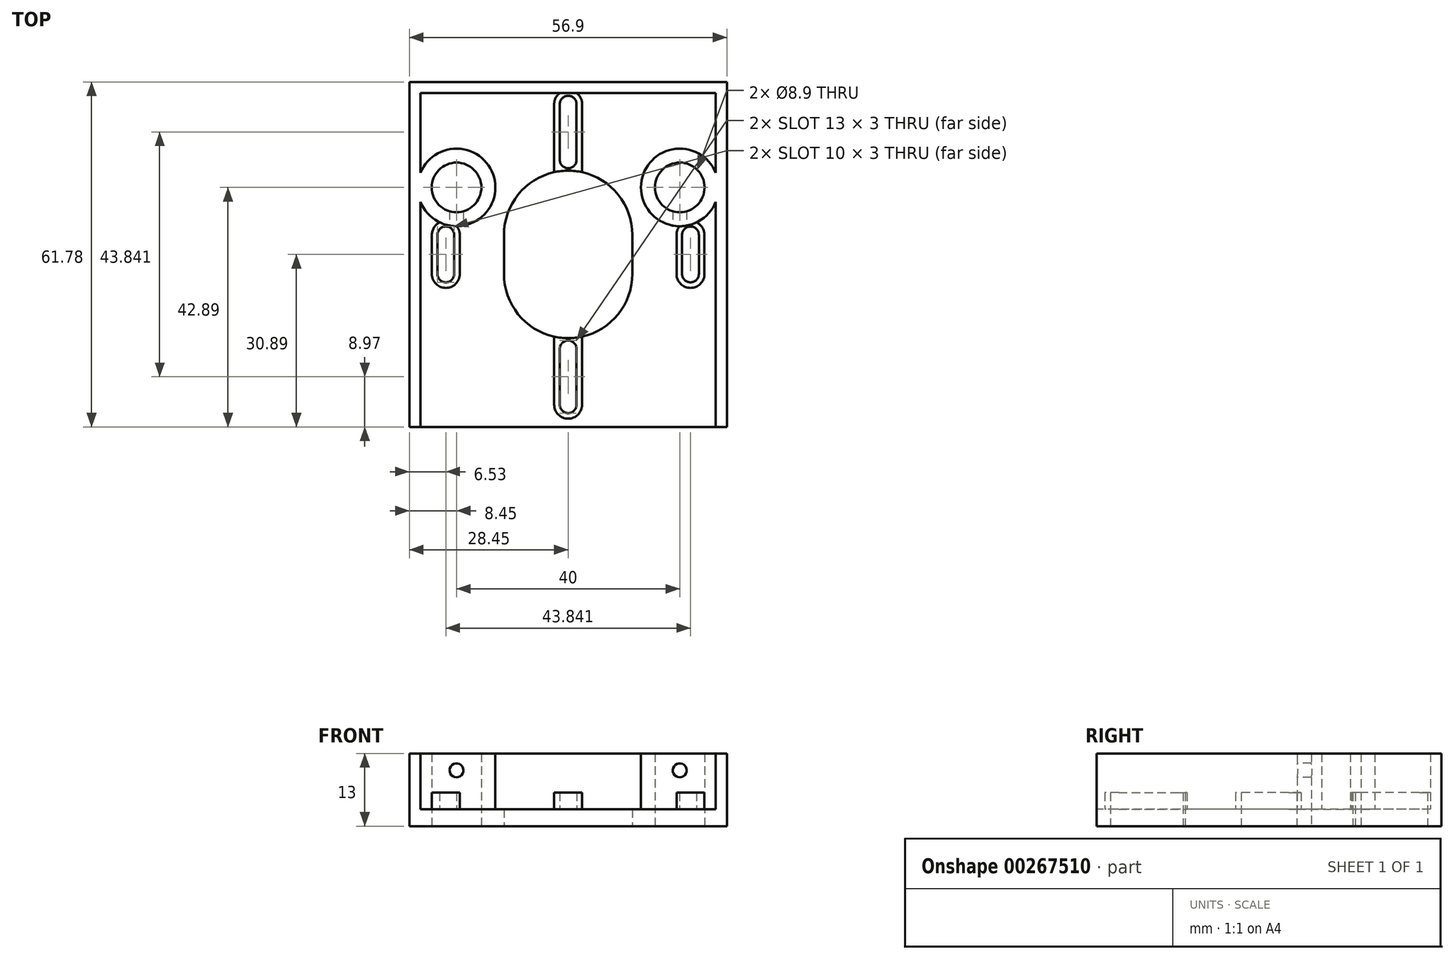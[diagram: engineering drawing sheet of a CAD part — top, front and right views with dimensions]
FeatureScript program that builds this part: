
annotation { "Feature Type Name" : "Feature", "Feature Type Description" : "" }
export const myFeature = defineFeature(function(context is Context, id is Id, definition is map)
    precondition{}
    {
        {
            var Q0;
            Q0=qCreatedBy(makeId("Top.planeOp"),FACE);
            var sketch = newSketch(context, id + "F0", { "sketchPlane" : qUnion([Q0])});
            skCircle(sketch, "E0", {"center": v(-20, 12) * mm, "radius": 4.45 * mm});
            skPoint(sketch, "E1.center", {"position": v(0, 0) * mm});
            skCircle(sketch, "E2.MirrorC", {"center": v(20, 12) * mm, "radius": 4.45 * mm});
            skLineSegment(sketch, "E3.bottom", {"start": v(28.45, 30.89) * mm, "end": v(-28.45, 30.89) * mm});
            skLineSegment(sketch, "E3.top", {"start": v(28.45, -30.89) * mm, "end": v(-28.45, -30.89) * mm});
            skLineSegment(sketch, "E3.left", {"start": v(28.45, 30.89) * mm, "end": v(28.45, -30.89) * mm});
            skLineSegment(sketch, "E3.right", {"start": v(-28.45, 30.89) * mm, "end": v(-28.45, -30.89) * mm});
            skLineSegment(sketch, "E4", {"start": v(-11.5, 0) * mm, "end": v(-11.5, 3.5) * mm});
            skArc(sketch, "E5", {"start": v(0, 15) * mm, "mid": v(-8.13, 11.63) * mm, "end": v(-11.5, 3.5) * mm});
            skLineSegment(sketch, "E6", {"start": v(-23.42, 0) * mm, "end": v(-23.42, 3.5) * mm});
            skLineSegment(sketch, "E7", {"start": v(-20.42, 0) * mm, "end": v(-20.42, 3.5) * mm});
            skArc(sketch, "E8", {"start": v(-20.42, 3.5) * mm, "mid": v(-21.92, 5) * mm, "end": v(-23.42, 3.5) * mm});
            skLineSegment(sketch, "E9", {"start": v(-1.5, 26.92) * mm, "end": v(-1.5, 16.92) * mm});
            skArc(sketch, "E10", {"start": v(0, 28.42) * mm, "mid": v(-1.06, 27.98) * mm, "end": v(-1.5, 26.92) * mm});
            skArc(sketch, "E11", {"start": v(-1.5, 16.92) * mm, "mid": v(-1.06, 15.86) * mm, "end": v(0, 15.42) * mm});
            skArc(sketch, "E12.MirrorCS", {"start": v(1.5, 16.92) * mm, "mid": v(1.06, 15.86) * mm, "end": v(0, 15.42) * mm});
            skLineSegment(sketch, "E13.MirrorCS", {"start": v(1.5, 26.92) * mm, "end": v(1.5, 16.92) * mm});
            skArc(sketch, "E14.MirrorCS", {"start": v(0, 28.42) * mm, "mid": v(1.06, 27.98) * mm, "end": v(1.5, 26.92) * mm});
            skLineSegment(sketch, "E15.MirrorCS", {"start": v(20.42, 0) * mm, "end": v(20.42, 3.5) * mm});
            skArc(sketch, "E16.MirrorCS", {"start": v(20.42, 3.5) * mm, "mid": v(21.92, 5) * mm, "end": v(23.42, 3.5) * mm});
            skLineSegment(sketch, "E17.MirrorCS", {"start": v(23.42, 0) * mm, "end": v(23.42, 3.5) * mm});
            skLineSegment(sketch, "E18.MirrorCS", {"start": v(11.5, 0) * mm, "end": v(11.5, 3.5) * mm});
            skArc(sketch, "E19.MirrorCS", {"start": v(0, 15) * mm, "mid": v(8.13, 11.63) * mm, "end": v(11.5, 3.5) * mm});
            skLineSegment(sketch, "E20.MirrorCS", {"start": v(-20.42, 0) * mm, "end": v(-20.42, -3.5) * mm});
            skArc(sketch, "E21.MirrorCS", {"start": v(-20.42, -3.5) * mm, "mid": v(-21.92, -5) * mm, "end": v(-23.42, -3.5) * mm});
            skLineSegment(sketch, "E22.MirrorCS", {"start": v(-23.42, 0) * mm, "end": v(-23.42, -3.5) * mm});
            skLineSegment(sketch, "E23.MirrorCS", {"start": v(-11.5, 0) * mm, "end": v(-11.5, -3.5) * mm});
            skArc(sketch, "E24.MirrorCS", {"start": v(0, -15) * mm, "mid": v(-8.13, -11.63) * mm, "end": v(-11.5, -3.5) * mm});
            skArc(sketch, "E25.MirrorCS", {"start": v(0, -15) * mm, "mid": v(8.13, -11.63) * mm, "end": v(11.5, -3.5) * mm});
            skLineSegment(sketch, "E26.MirrorCS", {"start": v(11.5, 0) * mm, "end": v(11.5, -3.5) * mm});
            skLineSegment(sketch, "E27.MirrorCS", {"start": v(20.42, 0) * mm, "end": v(20.42, -3.5) * mm});
            skArc(sketch, "E28.MirrorCS", {"start": v(20.42, -3.5) * mm, "mid": v(21.92, -5) * mm, "end": v(23.42, -3.5) * mm});
            skLineSegment(sketch, "E29.MirrorCS", {"start": v(23.42, 0) * mm, "end": v(23.42, -3.5) * mm});
            skLineSegment(sketch, "E30.MirrorCS", {"start": v(1.5, -26.92) * mm, "end": v(1.5, -16.92) * mm});
            skArc(sketch, "E31.MirrorCS", {"start": v(0, -28.42) * mm, "mid": v(1.06, -27.98) * mm, "end": v(1.5, -26.92) * mm});
            skArc(sketch, "E32.MirrorCS", {"start": v(0, -28.42) * mm, "mid": v(-1.06, -27.98) * mm, "end": v(-1.5, -26.92) * mm});
            skLineSegment(sketch, "E33.MirrorCS", {"start": v(-1.5, -26.92) * mm, "end": v(-1.5, -16.92) * mm});
            skArc(sketch, "E34.MirrorCS", {"start": v(-1.5, -16.92) * mm, "mid": v(-1.06, -15.86) * mm, "end": v(0, -15.42) * mm});
            skArc(sketch, "E35.MirrorCS", {"start": v(1.5, -16.92) * mm, "mid": v(1.06, -15.86) * mm, "end": v(0, -15.42) * mm});
            skLineSegment(sketch, "E36", {"start": v(-23.42, 0) * mm, "end": v(-20.42, 0) * mm, "construction": true});
            skLineSegment(sketch, "E37", {"start": v(-21.92, 0) * mm, "end": v(-21.92, 3.5) * mm, "construction": true});
            skLineSegment(sketch, "E38", {"start": v(-1.5, 21.92) * mm, "end": v(1.5, 21.92) * mm, "construction": true});
            skLineSegment(sketch, "E39", {"start": v(0, 21.92) * mm, "end": v(0, 16.92) * mm, "construction": true});
            skLineSegment(sketch, "E40", {"start": v(0, 0) * mm, "end": v(0, -21.92) * mm, "construction": true});
            skPoint(sketch, "E40.endSnap0", {"position": v(-1.5, -21.92) * mm});
            skLineSegment(sketch, "E41", {"start": v(0, 0) * mm, "end": v(21.92, 0) * mm, "construction": true});
            skSolve(sketch);
        }
        {
            var Q0;
            Q0 = qSketchRegion(id + "F0", true);
            extrude(context, id + "F1", {"entities" : qUnion([Q0]), "depth" : 3 * mm});
        }
        {
            var Q0;
            Q0=makeQuery(id+"F1.opExtrude","CAP_FACE",FACE,{"disambiguationData":[OSD([sQuery(id+"F0.wireOp",EDGE,"tHvmZrod-7iqJ-YdrQ-xS2p-iPQ9RPUyXmoZ"),sQuery(id+"F0.wireOp",EDGE,"ZnkVBOmS-lBIt-Q7PV-aiio-OzcAN4d0Z9aa"),sQuery(id+"F0.wireOp",EDGE,"h6YsiZyj-8vhA-jTGh-mmyY-8tryK31W9ES6.bottom"),sQuery(id+"F0.wireOp",EDGE,"h6YsiZyj-8vhA-jTGh-mmyY-8tryK31W9ES6.top"),sQuery(id+"F0.wireOp",EDGE,"h6YsiZyj-8vhA-jTGh-mmyY-8tryK31W9ES6.left"),sQuery(id+"F0.wireOp",EDGE,"h6YsiZyj-8vhA-jTGh-mmyY-8tryK31W9ES6.right"),sQuery(id+"F0.wireOp",EDGE,"E0"),sQuery(id+"F0.wireOp",EDGE,"E1.1.0"),sQuery(id+"F0.wireOp",EDGE,"E1.2.0"),sQuery(id+"F0.wireOp",EDGE,"E1.3.0"),sQuery(id+"F0.wireOp",EDGE,"E2.MirrorC")])],"isStart":false});
            var sketch = newSketch(context, id + "F2", { "sketchPlane" : qUnion([Q0])});
            skArc(sketch, "E42", {"start": v(-26.45, 9.41) * mm, "mid": v(-13.05, 12) * mm, "end": v(-26.45, 14.59) * mm});
            skCircle(sketch, "E43", {"center": v(-20, 12) * mm, "radius": 4.45 * mm});
            skArc(sketch, "E44.MirrorC", {"start": v(26.45, 9.41) * mm, "mid": v(13.05, 12) * mm, "end": v(26.45, 14.59) * mm});
            skCircle(sketch, "E45.MirrorC", {"center": v(20, 12) * mm, "radius": 4.45 * mm});
            skLineSegment(sketch, "E46", {"start": v(-28.45, -30.89) * mm, "end": v(-28.45, 30.89) * mm});
            skLineSegment(sketch, "E47", {"start": v(-28.45, 30.89) * mm, "end": v(28.45, 30.89) * mm});
            skLineSegment(sketch, "E48", {"start": v(28.45, 30.89) * mm, "end": v(28.45, -30.89) * mm});
            skLineSegment(sketch, "E49", {"start": v(28.45, -30.89) * mm, "end": v(26.45, -30.89) * mm});
            skLineSegment(sketch, "E50", {"start": v(26.45, -30.89) * mm, "end": v(26.45, 9.41) * mm});
            skLineSegment(sketch, "E51", {"start": v(26.45, 28.89) * mm, "end": v(-26.45, 28.89) * mm});
            skLineSegment(sketch, "E52", {"start": v(-26.45, 28.89) * mm, "end": v(-26.45, 14.59) * mm});
            skLineSegment(sketch, "E53", {"start": v(-26.45, -30.89) * mm, "end": v(-28.45, -30.89) * mm});
            skLineSegment(sketch, "E54", {"start": v(26.45, 28.89) * mm, "end": v(26.45, 30.89) * mm, "construction": true});
            skLineSegment(sketch, "E55.trimOffspring", {"start": v(-26.45, 9.41) * mm, "end": v(-26.45, -30.89) * mm});
            skLineSegment(sketch, "E56.trimOffspring", {"start": v(26.45, 14.59) * mm, "end": v(26.45, 28.89) * mm});
            skSolve(sketch);
        }
        {
            var Q0;
            Q0=makeQuery(id+"F1.opExtrude","CAP_FACE",FACE,{"disambiguationData":[OSD([sQuery(id+"F0.wireOp",EDGE,"E0"),sQuery(id+"F0.wireOp",EDGE,"E2.MirrorC"),sQuery(id+"F0.wireOp",EDGE,"E3.bottom"),sQuery(id+"F0.wireOp",EDGE,"E3.top"),sQuery(id+"F0.wireOp",EDGE,"E3.left"),sQuery(id+"F0.wireOp",EDGE,"E3.right"),sQuery(id+"F0.wireOp",EDGE,"E4"),sQuery(id+"F0.wireOp",EDGE,"E5"),sQuery(id+"F0.wireOp",EDGE,"E6"),sQuery(id+"F0.wireOp",EDGE,"E7"),sQuery(id+"F0.wireOp",EDGE,"E8"),sQuery(id+"F0.wireOp",EDGE,"E9"),sQuery(id+"F0.wireOp",EDGE,"E10"),sQuery(id+"F0.wireOp",EDGE,"E11"),sQuery(id+"F0.wireOp",EDGE,"E12.MirrorCS"),sQuery(id+"F0.wireOp",EDGE,"E13.MirrorCS"),sQuery(id+"F0.wireOp",EDGE,"E14.MirrorCS"),sQuery(id+"F0.wireOp",EDGE,"E15.MirrorCS"),sQuery(id+"F0.wireOp",EDGE,"E16.MirrorCS"),sQuery(id+"F0.wireOp",EDGE,"E17.MirrorCS"),sQuery(id+"F0.wireOp",EDGE,"E18.MirrorCS"),sQuery(id+"F0.wireOp",EDGE,"E19.MirrorCS"),sQuery(id+"F0.wireOp",EDGE,"E20.MirrorCS"),sQuery(id+"F0.wireOp",EDGE,"E21.MirrorCS"),sQuery(id+"F0.wireOp",EDGE,"E22.MirrorCS"),sQuery(id+"F0.wireOp",EDGE,"E23.MirrorCS"),sQuery(id+"F0.wireOp",EDGE,"E24.MirrorCS"),sQuery(id+"F0.wireOp",EDGE,"E25.MirrorCS"),sQuery(id+"F0.wireOp",EDGE,"E26.MirrorCS"),sQuery(id+"F0.wireOp",EDGE,"E27.MirrorCS"),sQuery(id+"F0.wireOp",EDGE,"E28.MirrorCS"),sQuery(id+"F0.wireOp",EDGE,"E29.MirrorCS"),sQuery(id+"F0.wireOp",EDGE,"E30.MirrorCS"),sQuery(id+"F0.wireOp",EDGE,"E31.MirrorCS"),sQuery(id+"F0.wireOp",EDGE,"E32.MirrorCS"),sQuery(id+"F0.wireOp",EDGE,"E33.MirrorCS"),sQuery(id+"F0.wireOp",EDGE,"E34.MirrorCS"),sQuery(id+"F0.wireOp",EDGE,"E35.MirrorCS")])],"isStart":false});
            var sketch = newSketch(context, id + "F3", { "sketchPlane" : qUnion([Q0])});
            skLineSegment(sketch, "E57.0", {"start": v(-24.42, 3.5) * mm, "end": v(-24.42, -3.5) * mm});
            skArc(sketch, "E57.1", {"start": v(-19.42, 3.5) * mm, "mid": v(-21.92, 6) * mm, "end": v(-24.42, 3.5) * mm});
            skLineSegment(sketch, "E57.2", {"start": v(-19.42, 3.5) * mm, "end": v(-19.42, -3.5) * mm});
            skArc(sketch, "E57.3", {"start": v(-19.42, -3.5) * mm, "mid": v(-21.92, -6) * mm, "end": v(-24.42, -3.5) * mm});
            skArc(sketch, "E58.0", {"start": v(-20.42, 3.5) * mm, "mid": v(-21.92, 5) * mm, "end": v(-23.42, 3.5) * mm});
            skLineSegment(sketch, "E58.1", {"start": v(-20.42, 3.5) * mm, "end": v(-20.42, -3.5) * mm});
            skArc(sketch, "E58.2", {"start": v(-20.42, -3.5) * mm, "mid": v(-21.92, -5) * mm, "end": v(-23.42, -3.5) * mm});
            skLineSegment(sketch, "E58.3", {"start": v(-23.42, 3.5) * mm, "end": v(-23.42, -3.5) * mm});
            skArc(sketch, "E59.0", {"start": v(2.5, 26.92) * mm, "mid": v(0, 29.42) * mm, "end": v(-2.5, 26.92) * mm});
            skLineSegment(sketch, "E59.1", {"start": v(2.5, 26.92) * mm, "end": v(2.5, 16.92) * mm});
            skLineSegment(sketch, "E59.3", {"start": v(-2.5, 26.92) * mm, "end": v(-2.5, 16.92) * mm});
            skLineSegment(sketch, "E60.0", {"start": v(-1.5, 26.92) * mm, "end": v(-1.5, 16.92) * mm});
            skArc(sketch, "E60.1", {"start": v(1.5, 26.92) * mm, "mid": v(0, 28.42) * mm, "end": v(-1.5, 26.92) * mm});
            skLineSegment(sketch, "E60.2", {"start": v(1.5, 26.92) * mm, "end": v(1.5, 16.92) * mm});
            skArc(sketch, "E60.3", {"start": v(1.5, 16.92) * mm, "mid": v(0, 15.42) * mm, "end": v(-1.5, 16.92) * mm});
            skLineSegment(sketch, "E61.MirrorCS", {"start": v(24.42, 3.5) * mm, "end": v(24.42, -3.5) * mm});
            skArc(sketch, "E62.MirrorCS", {"start": v(19.42, 3.5) * mm, "mid": v(21.92, 6) * mm, "end": v(24.42, 3.5) * mm});
            skLineSegment(sketch, "E63.MirrorCS", {"start": v(23.42, 3.5) * mm, "end": v(23.42, -3.5) * mm});
            skArc(sketch, "E64.MirrorCS", {"start": v(20.42, 3.5) * mm, "mid": v(21.92, 5) * mm, "end": v(23.42, 3.5) * mm});
            skLineSegment(sketch, "E65.MirrorCS", {"start": v(20.42, 3.5) * mm, "end": v(20.42, -3.5) * mm});
            skLineSegment(sketch, "E66.MirrorCS", {"start": v(19.42, 3.5) * mm, "end": v(19.42, -3.5) * mm});
            skArc(sketch, "E67.MirrorCS", {"start": v(19.42, -3.5) * mm, "mid": v(21.92, -6) * mm, "end": v(24.42, -3.5) * mm});
            skArc(sketch, "E68.MirrorCS", {"start": v(20.42, -3.5) * mm, "mid": v(21.92, -5) * mm, "end": v(23.42, -3.5) * mm});
            skArc(sketch, "E69.MirrorCS", {"start": v(2.5, -26.92) * mm, "mid": v(0, -29.42) * mm, "end": v(-2.5, -26.92) * mm});
            skArc(sketch, "E70.MirrorCS", {"start": v(1.5, -26.92) * mm, "mid": v(0, -28.42) * mm, "end": v(-1.5, -26.92) * mm});
            skLineSegment(sketch, "E71.MirrorCS", {"start": v(-2.5, -26.92) * mm, "end": v(-2.5, -16.92) * mm});
            skLineSegment(sketch, "E72.MirrorCS", {"start": v(-1.5, -26.92) * mm, "end": v(-1.5, -16.92) * mm});
            skLineSegment(sketch, "E73.MirrorCS", {"start": v(1.5, -26.92) * mm, "end": v(1.5, -16.92) * mm});
            skLineSegment(sketch, "E74.MirrorCS", {"start": v(2.5, -26.92) * mm, "end": v(2.5, -16.92) * mm});
            skArc(sketch, "E75.MirrorCS", {"start": v(1.5, -16.92) * mm, "mid": v(0, -15.42) * mm, "end": v(-1.5, -16.92) * mm});
            skLineSegment(sketch, "E76", {"start": v(-2.5, 16.92) * mm, "end": v(-2.5, 14.72) * mm});
            skLineSegment(sketch, "E77", {"start": v(2.5, 16.92) * mm, "end": v(2.5, 14.72) * mm});
            skArc(sketch, "E78", {"start": v(2.5, 14.72) * mm, "mid": v(0, 15) * mm, "end": v(-2.5, 14.72) * mm});
            skLineSegment(sketch, "E79.MirrorCS", {"start": v(-2.5, -16.92) * mm, "end": v(-2.5, -14.72) * mm});
            skArc(sketch, "E80.MirrorCS", {"start": v(2.5, -14.72) * mm, "mid": v(0, -15) * mm, "end": v(-2.5, -14.72) * mm});
            skLineSegment(sketch, "E81.MirrorCS", {"start": v(2.5, -16.92) * mm, "end": v(2.5, -14.72) * mm});
            skSolve(sketch);
        }
        {
            var Q0;
            Q0 = qSketchRegion(id + "F2", true);
            extrude(context, id + "F4", {"entities" : qUnion([Q0]), "operationType" : NewBodyOperationType.ADD, "depth" : 10 * mm});
        }
        {
            var Q0;
            Q0 = qSketchRegion(id + "F3", true);
            extrude(context, id + "F5", {"entities" : qUnion([Q0]), "operationType" : NewBodyOperationType.ADD, "depth" : 3 * mm});
        }
        {
            var Q0;
            Q0=makeQuery(id+"F4.boolean.opBoolean","MERGE",FACE,{"derivedFrom":[makeQuery(id+"F1.opExtrude","SWEPT_FACE",FACE,{"disambiguationData":[OSD([sQuery(id+"F0.wireOp",EDGE,"E3.top")])]}),makeQuery(id+"F4.opExtrude","SWEPT_FACE",FACE,{"disambiguationData":[OSD([sQuery(id+"F2.wireOp",EDGE,"E49")])]}),makeQuery(id+"F4.opExtrude","SWEPT_FACE",FACE,{"disambiguationData":[OSD([sQuery(id+"F2.wireOp",EDGE,"E53")])]})]});
            var sketch = newSketch(context, id + "F6", { "sketchPlane" : qUnion([Q0])});
            skCircle(sketch, "E82", {"center": v(-20, 10) * mm, "radius": 1.25 * mm});
            skCircle(sketch, "E83.MirrorC", {"center": v(20, 10) * mm, "radius": 1.25 * mm});
            skSolve(sketch);
        }
        {
            var Q0;
            Q0 = qSketchRegion(id + "F6", true);
            extrude(context, id + "F7", {"entities" : qUnion([Q0]), "operationType" : NewBodyOperationType.REMOVE, "oppositeDirection" : true, "depth" : 40 * mm});
        }
    });
